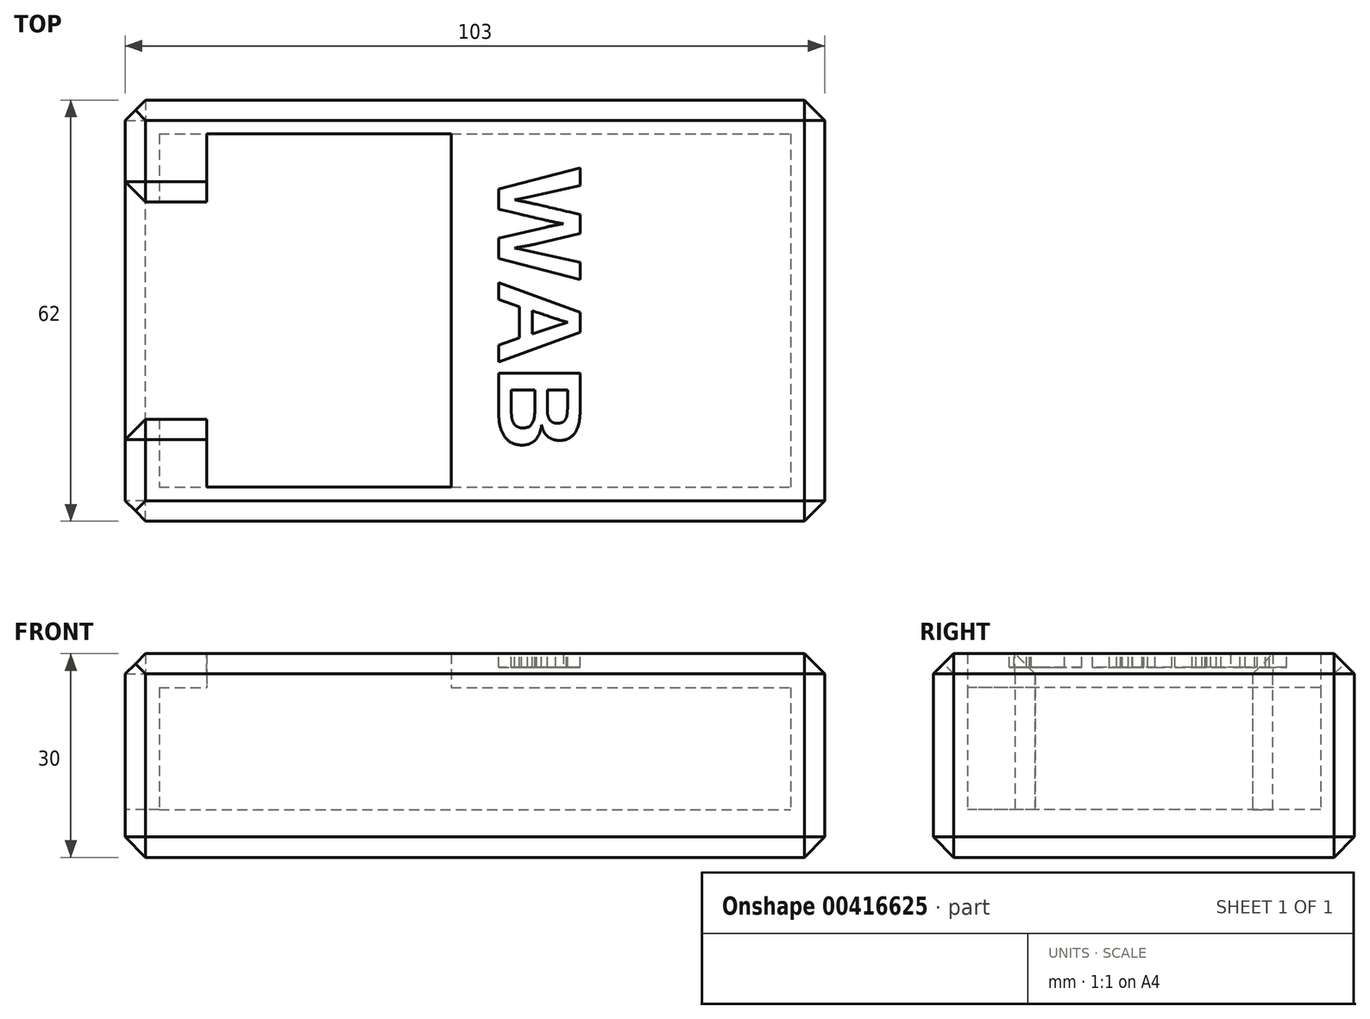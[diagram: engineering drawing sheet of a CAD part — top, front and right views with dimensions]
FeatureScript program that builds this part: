
annotation { "Feature Type Name" : "Feature", "Feature Type Description" : "" }
export const myFeature = defineFeature(function(context is Context, id is Id, definition is map)
    precondition{}
    {
        {
            var Q0;
            Q0=qCreatedBy(makeId("Top.planeOp"),FACE);
            var sketch = newSketch(context, id + "F0", { "sketchPlane" : qUnion([Q0])});
            skLineSegment(sketch, "E0.bottom", {"start": v(0, 0) * mm, "end": v(93, 0) * mm});
            skLineSegment(sketch, "E0.top", {"start": v(0, -52) * mm, "end": v(93, -52) * mm});
            skLineSegment(sketch, "E0.left", {"start": v(0, 0) * mm, "end": v(0, -52) * mm});
            skLineSegment(sketch, "E0.right", {"start": v(93, 0) * mm, "end": v(93, -52) * mm});
            skLineSegment(sketch, "E1.bottom", {"start": v(-5, 5) * mm, "end": v(98, 5) * mm});
            skLineSegment(sketch, "E1.top", {"start": v(-5, -57) * mm, "end": v(98, -57) * mm});
            skLineSegment(sketch, "E1.left", {"start": v(-5, 5) * mm, "end": v(-5, -57) * mm});
            skLineSegment(sketch, "E1.right", {"start": v(98, 5) * mm, "end": v(98, -57) * mm});
            skLineSegment(sketch, "E2.bottom", {"start": v(0, -10) * mm, "end": v(-5, -10) * mm});
            skLineSegment(sketch, "E2.top", {"start": v(0, -42) * mm, "end": v(-5, -42) * mm});
            skLineSegment(sketch, "E2.left", {"start": v(0, -10) * mm, "end": v(0, -42) * mm});
            skLineSegment(sketch, "E2.right", {"start": v(-5, -10) * mm, "end": v(-5, -42) * mm});
            skSolve(sketch);
        }
        {
            var Q0;
            {var subQ6=sQuery(id+"F0.wireOp",EDGE,"E0.bottom");Q0=makeQuery(id+"F0.imprint","IMPRINT",FACE,{"disambiguationData":[TD([[makeQuery(id+"F0.imprint","IMPRINT",EDGE,{"derivedFrom":subQ6}),1.0]])]});}
            extrude(context, id + "F1", {"entities" : qUnion([Q0]), "depth" : 25 * mm});
        }
        {
            var Q0;
            {var subQ3=sQuery(id+"F0.wireOp",EDGE,"E0.bottom");Q0=makeQuery(id+"F0.imprint","IMPRINT",FACE,{"disambiguationData":[TD([[makeQuery(id+"F0.imprint","IMPRINT",EDGE,{"derivedFrom":subQ3}),-1.0]])]});}
            extrude(context, id + "F2", {"entities" : qUnion([Q0]), "operationType" : NewBodyOperationType.ADD, "depth" : 7 * mm});
        }
        {
            var Q0;
            Q0=makeQuery(id+"F1.opExtrude","CAP_FACE",FACE,{"disambiguationData":[OSD([sQuery(id+"F0.wireOp",EDGE,"E0.bottom"),sQuery(id+"F0.wireOp",EDGE,"E0.top"),sQuery(id+"F0.wireOp",EDGE,"E0.left"),sQuery(id+"F0.wireOp",EDGE,"E0.right"),sQuery(id+"F0.wireOp",EDGE,"E1.bottom"),sQuery(id+"F0.wireOp",EDGE,"E1.top"),sQuery(id+"F0.wireOp",EDGE,"E1.left"),sQuery(id+"F0.wireOp",EDGE,"E1.right"),sQuery(id+"F0.wireOp",EDGE,"E2.bottom"),sQuery(id+"F0.wireOp",EDGE,"E2.top")])],"isStart":false});
            var sketch = newSketch(context, id + "F3", { "sketchPlane" : qUnion([Q0])});
            skPoint(sketch, "E3.oppositeSnap0", {"position": v(-2.5, -10) * mm});
            skLineSegment(sketch, "E3.bottom", {"start": v(-5, 5) * mm, "end": v(7, 5) * mm});
            skLineSegment(sketch, "E3.top", {"start": v(-5, -10) * mm, "end": v(7, -10) * mm});
            skLineSegment(sketch, "E3.left", {"start": v(-5, 5) * mm, "end": v(-5, -10) * mm});
            skLineSegment(sketch, "E3.right", {"start": v(7, 5) * mm, "end": v(7, -10) * mm});
            skLineSegment(sketch, "E4.bottom", {"start": v(-5, -57) * mm, "end": v(7, -57) * mm});
            skLineSegment(sketch, "E4.top", {"start": v(-5, -42) * mm, "end": v(7, -42) * mm});
            skLineSegment(sketch, "E4.left", {"start": v(-5, -57) * mm, "end": v(-5, -42) * mm});
            skLineSegment(sketch, "E4.right", {"start": v(7, -57) * mm, "end": v(7, -42) * mm});
            skLineSegment(sketch, "E5.bottom", {"start": v(98, 5) * mm, "end": v(43, 5) * mm});
            skLineSegment(sketch, "E5.top", {"start": v(98, -57) * mm, "end": v(43, -57) * mm});
            skLineSegment(sketch, "E5.left", {"start": v(98, 5) * mm, "end": v(98, -57) * mm});
            skLineSegment(sketch, "E5.right", {"start": v(43, 5) * mm, "end": v(43, -57) * mm});
            skSolve(sketch);
        }
        {
            var Q0;
            Q0 = qSketchRegion(id + "F3", true);
            var Q1;
            {var subQ0=sQuery(id+"F3.wireOp",EDGE,"E3.right");var subQ3=makeQuery(id+"F1.opExtrude","CAP_EDGE",EDGE,{"disambiguationData":[OSD([sQuery(id+"F0.wireOp",EDGE,"E0.bottom")])],"isStart":false});var subQ4=makeQuery(id+"F3.imprint","INTERSECT",VERTEX,{"derivedFrom":[subQ3,subQ0]});Q1=makeQuery(id+"F3.imprint","IMPRINT",FACE,{"disambiguationData":[TD([[makeQuery(id+"F3.imprint","IMPRINT",EDGE,{"disambiguationData":[TD([[subQ4,-1.0]])],"derivedFrom":subQ3}),1.0]])]});}
            var Q2;
            {var subQ0=sQuery(id+"F3.wireOp",EDGE,"E4.right");var subQ3=makeQuery(id+"F1.opExtrude","CAP_EDGE",EDGE,{"disambiguationData":[OSD([sQuery(id+"F0.wireOp",EDGE,"E0.top")])],"isStart":false});var subQ4=makeQuery(id+"F3.imprint","INTERSECT",VERTEX,{"derivedFrom":[subQ3,subQ0]});Q2=makeQuery(id+"F3.imprint","IMPRINT",FACE,{"disambiguationData":[TD([[makeQuery(id+"F3.imprint","IMPRINT",EDGE,{"disambiguationData":[TD([[subQ4,-1.0]])],"derivedFrom":subQ3}),-1.0]])]});}
            extrude(context, id + "F4", {"entities" : qUnion([Q0, Q1, Q2]), "operationType" : NewBodyOperationType.ADD, "depth" : 5 * mm});
        }
        {
            var Q0;
            Q0=makeQuery(id+"F0.imprint","IMPRINT",FACE,{"disambiguationData":[TD([[makeQuery(id+"F0.imprint","IMPRINT",EDGE,{"derivedFrom":sQuery(id+"F0.wireOp",EDGE,"E2.bottom")}),1.0]])]});
            extrude(context, id + "F5", {"entities" : qUnion([Q0]), "operationType" : NewBodyOperationType.ADD, "depth" : 7 * mm});
        }
        {
            var Q0;
            Q0=makeQuery(id+"F4.opExtrude","CAP_EDGE",EDGE,{"disambiguationData":[OSD([sQuery(id+"F0.wireOp",EDGE,"E1.top"),sQuery(id+"F3.wireOp",EDGE,"E4.bottom"),sQuery(id+"F3.wireOp",EDGE,"E5.top")])],"isStart":false});
            var Q1;
            Q1=makeQuery(id+"F1.opExtrude","CAP_EDGE",EDGE,{"disambiguationData":[OSD([sQuery(id+"F0.wireOp",EDGE,"E1.top")])],"isStart":true});
            var Q2;
            Q2=makeQuery(id+"F4.boolean.opBoolean","MERGE",EDGE,{"derivedFrom":[makeQuery(id+"F1.opExtrude","SWEPT_EDGE",EDGE,{"disambiguationData":[OSD([sQuery(id+"F0.wireOp",EDGE,"E1.top"),sQuery(id+"F0.wireOp",EDGE,"E1.left")])]}),makeQuery(id+"F4.opExtrude","SWEPT_EDGE",EDGE,{"disambiguationData":[OSD([sQuery(id+"F3.wireOp",EDGE,"E4.bottom"),sQuery(id+"F3.wireOp",EDGE,"E4.left")])]})]});
            var Q3;
            Q3=makeQuery(id+"F4.boolean.opBoolean","MERGE",EDGE,{"derivedFrom":[makeQuery(id+"F1.opExtrude","SWEPT_EDGE",EDGE,{"disambiguationData":[OSD([sQuery(id+"F0.wireOp",EDGE,"E1.top"),sQuery(id+"F0.wireOp",EDGE,"E1.right")])]}),makeQuery(id+"F4.opExtrude","SWEPT_EDGE",EDGE,{"disambiguationData":[OSD([sQuery(id+"F3.wireOp",EDGE,"E5.top"),sQuery(id+"F3.wireOp",EDGE,"E5.left")])]})]});
            var Q4;
            Q4=makeQuery(id+"F4.boolean.opBoolean","MERGE",FACE,{"derivedFrom":[makeQuery(id+"F1.opExtrude","SWEPT_FACE",FACE,{"disambiguationData":[OSD([sQuery(id+"F0.wireOp",EDGE,"E1.right")])]}),makeQuery(id+"F4.opExtrude","SWEPT_FACE",FACE,{"disambiguationData":[OSD([sQuery(id+"F3.wireOp",EDGE,"E5.left")])]})]});
            var Q5;
            {var subQ0=sQuery(id+"F0.wireOp",EDGE,"E1.bottom");Q5=makeQuery(id+"F4.boolean.opBoolean","MERGE",FACE,{"derivedFrom":[makeQuery(id+"F1.opExtrude","SWEPT_FACE",FACE,{"disambiguationData":[OSD([subQ0])]}),makeQuery(id+"F4.opExtrude","SWEPT_FACE",FACE,{"disambiguationData":[OSD([subQ0,sQuery(id+"F3.wireOp",EDGE,"E3.bottom"),sQuery(id+"F3.wireOp",EDGE,"E5.bottom")])]})]});}
            var Q6;
            {var subQ0=sQuery(id+"F0.wireOp",EDGE,"E2.left");var subQ1=sQuery(id+"F0.wireOp",EDGE,"E2.top");var subQ2=sQuery(id+"F0.wireOp",EDGE,"E2.bottom");var subQ3=sQuery(id+"F0.wireOp",EDGE,"E0.right");var subQ4=sQuery(id+"F0.wireOp",EDGE,"E0.left");var subQ5=sQuery(id+"F0.wireOp",EDGE,"E0.top");var subQ6=sQuery(id+"F0.wireOp",EDGE,"E0.bottom");Q6=makeQuery(id+"F5.boolean.opBoolean","MERGE",FACE,{"derivedFrom":[makeQuery(id+"F2.boolean.opBoolean","MERGE",FACE,{"derivedFrom":[makeQuery(id+"F1.opExtrude","CAP_FACE",FACE,{"disambiguationData":[OSD([subQ6,subQ5,subQ4,subQ3,sQuery(id+"F0.wireOp",EDGE,"E1.bottom"),sQuery(id+"F0.wireOp",EDGE,"E1.top"),sQuery(id+"F0.wireOp",EDGE,"E1.left"),sQuery(id+"F0.wireOp",EDGE,"E1.right"),subQ2,subQ1])],"isStart":true}),makeQuery(id+"F2.opExtrude","CAP_FACE",FACE,{"disambiguationData":[OSD([subQ6,subQ5,subQ4,subQ3,subQ0])],"isStart":true})]}),makeQuery(id+"F5.opExtrude","CAP_FACE",FACE,{"disambiguationData":[OSD([subQ2,subQ1,subQ0,sQuery(id+"F0.wireOp",EDGE,"E2.right")])],"isStart":true})]});}
            chamfer(context, id + "F6", {"entities" : qUnion([Q0, Q1, Q2, Q3, Q4, Q5, Q6]), "width" : 3 * mm, "tangentPropagation" : true});
        }
        {
            var Q0;
            Q0=makeQuery(id+"F4.opExtrude","CAP_EDGE",EDGE,{"disambiguationData":[OSD([sQuery(id+"F3.wireOp",EDGE,"E3.left")])],"isStart":false});
            var Q1;
            Q1=makeQuery(id+"F4.opExtrude","CAP_EDGE",EDGE,{"disambiguationData":[OSD([sQuery(id+"F3.wireOp",EDGE,"E4.left")])],"isStart":false});
            var Q2;
            Q2=makeQuery(id+"F4.boolean.opBoolean","MERGE",EDGE,{"derivedFrom":[makeQuery(id+"F1.opExtrude","SWEPT_EDGE",EDGE,{"disambiguationData":[OSD([sQuery(id+"F0.wireOp",EDGE,"E1.left"),sQuery(id+"F0.wireOp",EDGE,"E2.bottom"),sQuery(id+"F0.wireOp",EDGE,"E2.right")])]}),makeQuery(id+"F4.opExtrude","SWEPT_EDGE",EDGE,{"disambiguationData":[OSD([sQuery(id+"F3.wireOp",EDGE,"E3.top"),sQuery(id+"F3.wireOp",EDGE,"E3.left")])]})]});
            var Q3;
            Q3=makeQuery(id+"F5.opExtrude","CAP_EDGE",EDGE,{"disambiguationData":[OSD([sQuery(id+"F0.wireOp",EDGE,"E2.right")])],"isStart":false});
            var Q4;
            Q4=makeQuery(id+"F4.boolean.opBoolean","MERGE",EDGE,{"derivedFrom":[makeQuery(id+"F1.opExtrude","SWEPT_EDGE",EDGE,{"disambiguationData":[OSD([sQuery(id+"F0.wireOp",EDGE,"E1.left"),sQuery(id+"F0.wireOp",EDGE,"E2.top"),sQuery(id+"F0.wireOp",EDGE,"E2.right")])]}),makeQuery(id+"F4.opExtrude","SWEPT_EDGE",EDGE,{"disambiguationData":[OSD([sQuery(id+"F3.wireOp",EDGE,"E4.top"),sQuery(id+"F3.wireOp",EDGE,"E4.left")])]})]});
            var Q5;
            Q5=makeQuery(id+"F4.opExtrude","CAP_EDGE",EDGE,{"disambiguationData":[OSD([sQuery(id+"F3.wireOp",EDGE,"E3.top")])],"isStart":false});
            var Q6;
            Q6=makeQuery(id+"F4.opExtrude","CAP_EDGE",EDGE,{"disambiguationData":[OSD([sQuery(id+"F3.wireOp",EDGE,"E4.top")])],"isStart":false});
            chamfer(context, id + "F7", {"entities" : qUnion([Q0, Q1, Q2, Q3, Q4, Q5, Q6]), "width" : 3 * mm, "tangentPropagation" : true});
        }
        {
            var Q0;
            Q0=makeQuery(id+"F4.opExtrude","CAP_FACE",FACE,{"disambiguationData":[OSD([sQuery(id+"F0.wireOp",EDGE,"E0.bottom"),sQuery(id+"F0.wireOp",EDGE,"E0.top"),sQuery(id+"F0.wireOp",EDGE,"E1.bottom"),sQuery(id+"F0.wireOp",EDGE,"E1.top"),sQuery(id+"F3.wireOp",EDGE,"E3.bottom"),sQuery(id+"F3.wireOp",EDGE,"E3.top"),sQuery(id+"F3.wireOp",EDGE,"E3.left"),sQuery(id+"F3.wireOp",EDGE,"E3.right"),sQuery(id+"F3.wireOp",EDGE,"E4.bottom"),sQuery(id+"F3.wireOp",EDGE,"E4.top"),sQuery(id+"F3.wireOp",EDGE,"E4.left"),sQuery(id+"F3.wireOp",EDGE,"E4.right"),sQuery(id+"F3.wireOp",EDGE,"E5.bottom"),sQuery(id+"F3.wireOp",EDGE,"E5.top"),sQuery(id+"F3.wireOp",EDGE,"E5.left"),sQuery(id+"F3.wireOp",EDGE,"E5.right")])],"isStart":false});
            var sketch = newSketch(context, id + "F8", { "sketchPlane" : qUnion([Q0])});
            skText(sketch, "E6", { "text": "WAB", "fontName": "Arimo-Bold.ttf"});
            const initialGuessF8  = {"E6": [0.05, -0.005, 0, -1, 0.01254]};
            skSetInitialGuess(sketch, initialGuessF8);
            skSolve(sketch);
        }
        {
            var Q0;
            Q0=makeQuery(id+"F8.imprint","IMPRINT",FACE,{"disambiguationData":[TD([[makeQuery(id+"F8.imprint","IMPRINT",EDGE,{"derivedFrom":sQuery(id+"F8.wireOp",EDGE,"E6.sketch_text.stroke-0")}),-1.0]])]});
            var Q1;
            Q1=makeQuery(id+"F8.imprint","IMPRINT",FACE,{"disambiguationData":[TD([[makeQuery(id+"F8.imprint","IMPRINT",EDGE,{"derivedFrom":sQuery(id+"F8.wireOp",EDGE,"E6.sketch_text.stroke-20")}),-1.0]])]});
            var Q2;
            Q2=makeQuery(id+"F8.imprint","IMPRINT",FACE,{"disambiguationData":[TD([[makeQuery(id+"F8.imprint","IMPRINT",EDGE,{"derivedFrom":sQuery(id+"F8.wireOp",EDGE,"E6.sketch_text.stroke-35")}),-1.0]])]});
            extrude(context, id + "F9", {"entities" : qUnion([Q0, Q1, Q2]), "operationType" : NewBodyOperationType.REMOVE, "oppositeDirection" : true, "depth" : 2 * mm});
        }
    });
